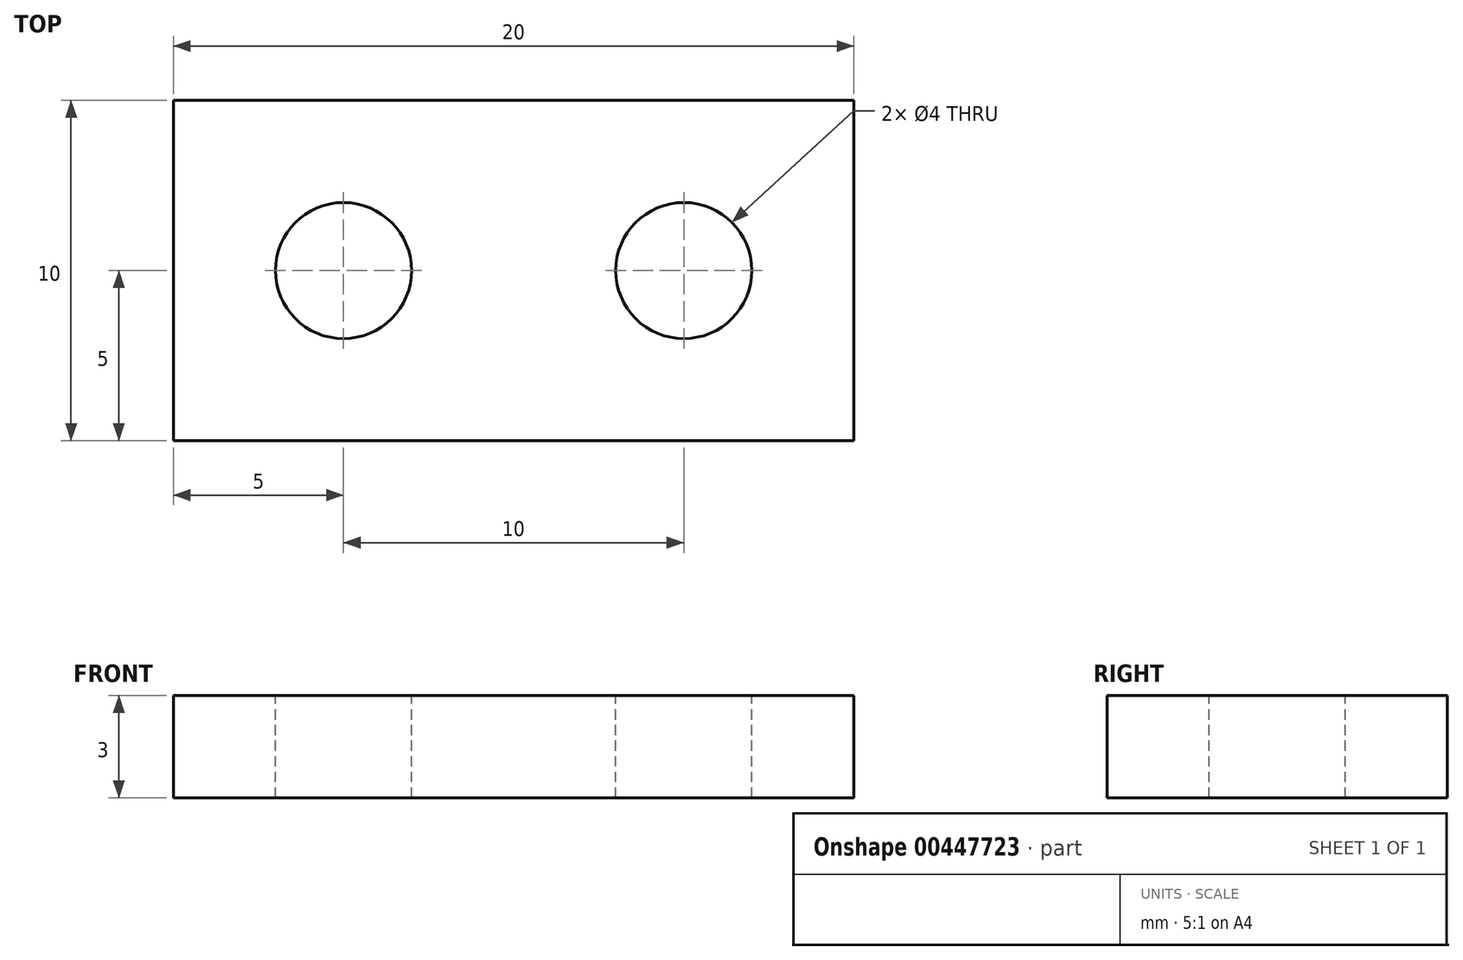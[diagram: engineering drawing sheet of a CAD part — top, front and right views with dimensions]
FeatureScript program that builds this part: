
annotation { "Feature Type Name" : "Feature", "Feature Type Description" : "" }
export const myFeature = defineFeature(function(context is Context, id is Id, definition is map)
    precondition{}
    {
        {
            var Q0;
            Q0=qCreatedBy(makeId("Top.planeOp"),FACE);
            var sketch = newSketch(context, id + "F0", { "sketchPlane" : qUnion([Q0])});
            skLineSegment(sketch, "E0.bottom", {"start": v(-10, 5) * mm, "end": v(10, 5) * mm});
            skLineSegment(sketch, "E0.top", {"start": v(-10, -5) * mm, "end": v(10, -5) * mm});
            skLineSegment(sketch, "E0.left", {"start": v(-10, 5) * mm, "end": v(-10, -5) * mm});
            skLineSegment(sketch, "E0.right", {"start": v(10, 5) * mm, "end": v(10, -5) * mm});
            skPoint(sketch, "E0.middle", {"position": v(0, 0) * mm});
            skSolve(sketch);
        }
        {
            var Q0;
            Q0 = qSketchRegion(id + "F0", true);
            extrude(context, id + "F1", {"entities" : qUnion([Q0]), "depth" : 3 * mm, "offsetDistance" : 25 * mm});
        }
        {
            var Q0;
            Q0=makeQuery(id+"F1.opExtrude","CAP_FACE",FACE,{"disambiguationData":[OSD([sQuery(id+"F0.wireOp",EDGE,"E0.bottom"),sQuery(id+"F0.wireOp",EDGE,"E0.top"),sQuery(id+"F0.wireOp",EDGE,"E0.left"),sQuery(id+"F0.wireOp",EDGE,"E0.right")])],"isStart":false});
            var sketch = newSketch(context, id + "F2", { "sketchPlane" : qUnion([Q0])});
            skLineSegment(sketch, "E1", {"start": v(-10, 0) * mm, "end": v(0, 0) * mm});
            skLineSegment(sketch, "E2", {"start": v(0, 0) * mm, "end": v(10, 0) * mm});
            skCircle(sketch, "E3", {"center": v(-5, 0) * mm, "radius": 2 * mm});
            skCircle(sketch, "E4", {"center": v(5, 0) * mm, "radius": 2 * mm});
            skSolve(sketch);
        }
        {
            var Q0;
            Q0 = qSketchRegion(id + "F2", true);
            extrude(context, id + "F3", {"entities" : qUnion([Q0]), "operationType" : NewBodyOperationType.REMOVE, "oppositeDirection" : true, "depth" : 3 * mm, "offsetDistance" : 25 * mm});
        }
    });
